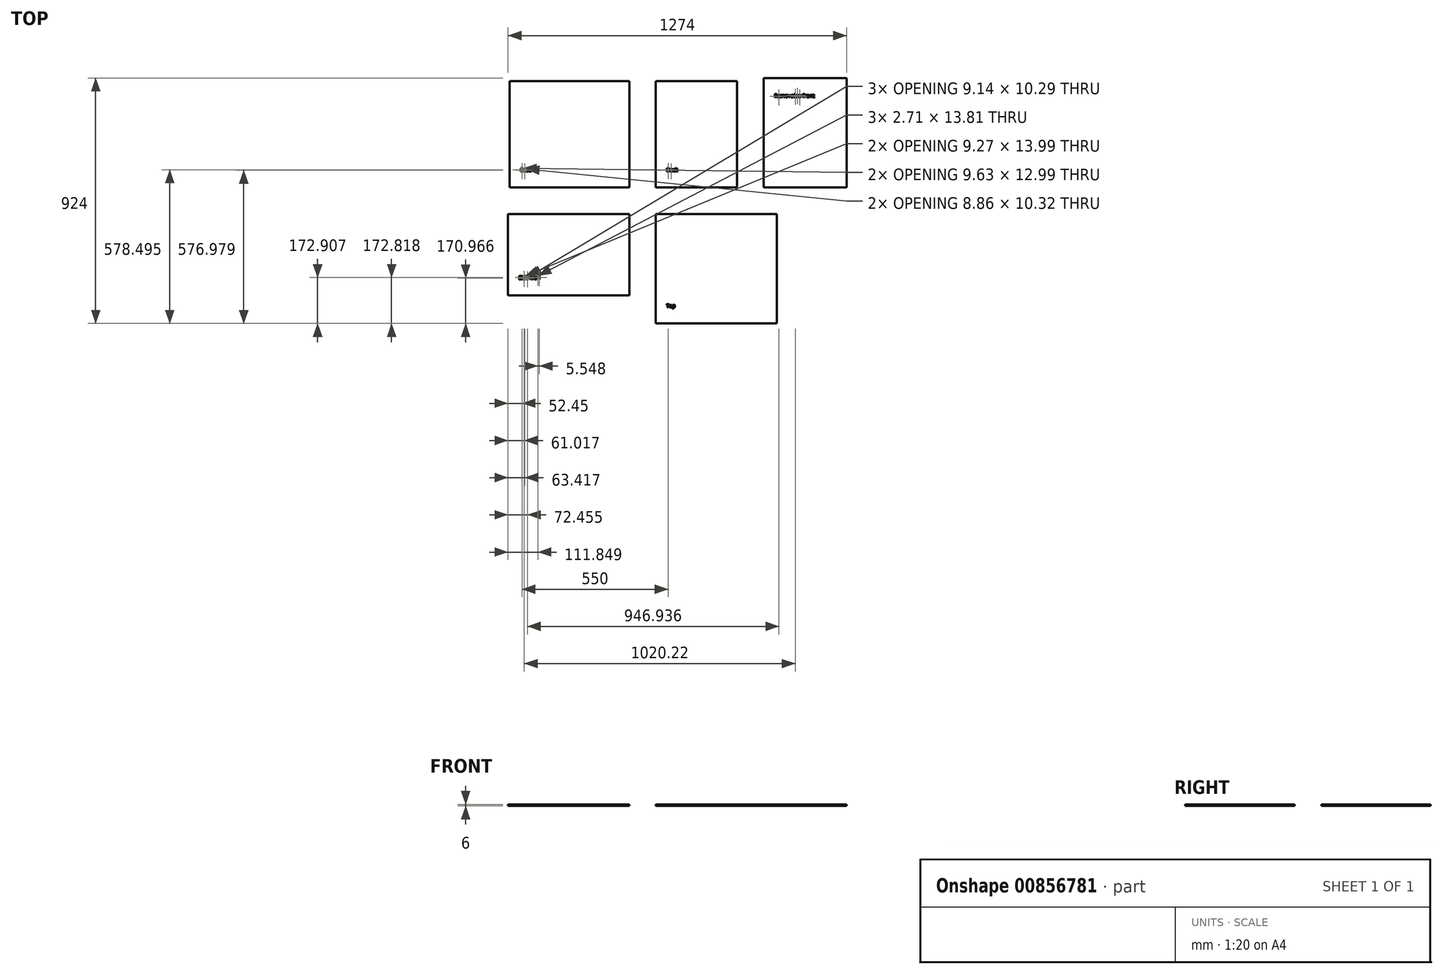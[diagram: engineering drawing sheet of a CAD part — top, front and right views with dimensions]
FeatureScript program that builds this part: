
annotation { "Feature Type Name" : "Feature", "Feature Type Description" : "" }
export const myFeature = defineFeature(function(context is Context, id is Id, definition is map)
    precondition{}
    {
        {
            var Q0;
            Q0=qCreatedBy(makeId("Top.planeOp"),FACE);
            var sketch = newSketch(context, id + "F0", { "sketchPlane" : qUnion([Q0])});
            skLineSegment(sketch, "E0.bottom", {"start": v(-50, 50) * mm, "end": v(-500, 50) * mm});
            skLineSegment(sketch, "E0.top", {"start": v(-50, 450) * mm, "end": v(-500, 450) * mm});
            skLineSegment(sketch, "E0.left", {"start": v(-50, 50) * mm, "end": v(-50, 450) * mm});
            skLineSegment(sketch, "E0.right", {"start": v(-500, 50) * mm, "end": v(-500, 450) * mm});
            skLineSegment(sketch, "E1.bottom", {"start": v(50, 50) * mm, "end": v(356, 50) * mm});
            skLineSegment(sketch, "E1.top", {"start": v(50, 450) * mm, "end": v(356, 450) * mm});
            skLineSegment(sketch, "E1.left", {"start": v(50, 50) * mm, "end": v(50, 450) * mm});
            skLineSegment(sketch, "E1.right", {"start": v(356, 50) * mm, "end": v(356, 450) * mm});
            skLineSegment(sketch, "E2.bottom", {"start": v(-50, -50) * mm, "end": v(-506, -50) * mm});
            skLineSegment(sketch, "E2.top", {"start": v(-50, -356) * mm, "end": v(-506, -356) * mm});
            skLineSegment(sketch, "E2.left", {"start": v(-50, -50) * mm, "end": v(-50, -356) * mm});
            skLineSegment(sketch, "E2.right", {"start": v(-506, -50) * mm, "end": v(-506, -356) * mm});
            skLineSegment(sketch, "E3.bottom", {"start": v(50, -50) * mm, "end": v(506, -50) * mm});
            skLineSegment(sketch, "E3.top", {"start": v(50, -462) * mm, "end": v(506, -462) * mm});
            skLineSegment(sketch, "E3.left", {"start": v(50, -50) * mm, "end": v(50, -462) * mm});
            skLineSegment(sketch, "E3.right", {"start": v(506, -50) * mm, "end": v(506, -462) * mm});
            skLineSegment(sketch, "E4", {"start": v(396, 50) * mm, "end": v(396, 60) * mm, "construction": true});
            skText(sketch, "E5", { "text": "Back", "fontName": "OpenSans-Bold.ttf"});
            skText(sketch, "E6", { "text": "Side wall", "fontName": "OpenSans-Bold.ttf"});
            skText(sketch, "E7", { "text": "Base", "fontName": "OpenSans-Bold.ttf"});
            skText(sketch, "E8", { "text": "Top", "fontName": "OpenSans-Bold.ttf"});
            skLineSegment(sketch, "E9.bottom", {"start": v(456, 50) * mm, "end": v(768, 50) * mm});
            skLineSegment(sketch, "E9.top", {"start": v(456, 462) * mm, "end": v(768, 462) * mm});
            skLineSegment(sketch, "E9.left", {"start": v(456, 50) * mm, "end": v(456, 462) * mm});
            skLineSegment(sketch, "E9.right", {"start": v(768, 50) * mm, "end": v(768, 462) * mm});
            skText(sketch, "E10", { "text": "Removable front", "fontName": "OpenSans-Bold.ttf"});
            const initialGuessF0  = {"E5": [0.09, 0.11, 1, 0, 0.0131], "E6": [-0.466, -0.296, 1, 0, 0.01309], "E7": [-0.46, 0.11, 1, 0, 0.0131], "E8": [0.09, -0.402, 1, 0, 0.0131], "E10": [0.496, 0.38891, 1, 0, 0.01309]};
            skSetInitialGuess(sketch, initialGuessF0);
            skSolve(sketch);
        }
        {
            var Q0;
            Q0=makeQuery(id+"F0.imprint","IMPRINT",FACE,{"disambiguationData":[TD([[makeQuery(id+"F0.imprint","IMPRINT",EDGE,{"derivedFrom":sQuery(id+"F0.wireOp",EDGE,"E0.bottom")}),-1.0]])]});
            extrude(context, id + "F1", {"entities" : qUnion([Q0]), "depth" : 6 * mm, "offsetDistance" : 25 * mm});
        }
        {
            var Q0;
            Q0=makeQuery(id+"F0.imprint","IMPRINT",FACE,{"disambiguationData":[TD([[makeQuery(id+"F0.imprint","IMPRINT",EDGE,{"derivedFrom":sQuery(id+"F0.wireOp",EDGE,"E1.bottom")}),1.0]])]});
            extrude(context, id + "F2", {"entities" : qUnion([Q0]), "depth" : 6 * mm, "offsetDistance" : 25 * mm});
        }
        {
            var Q0;
            Q0=makeQuery(id+"F0.imprint","IMPRINT",FACE,{"disambiguationData":[TD([[makeQuery(id+"F0.imprint","IMPRINT",EDGE,{"derivedFrom":sQuery(id+"F0.wireOp",EDGE,"E2.bottom")}),1.0]])]});
            extrude(context, id + "F3", {"entities" : qUnion([Q0]), "depth" : 6 * mm, "offsetDistance" : 25 * mm});
        }
        {
            var Q0;
            Q0=makeQuery(id+"F0.imprint","IMPRINT",FACE,{"disambiguationData":[TD([[makeQuery(id+"F0.imprint","IMPRINT",EDGE,{"derivedFrom":sQuery(id+"F0.wireOp",EDGE,"E3.bottom")}),-1.0]])]});
            extrude(context, id + "F4", {"entities" : qUnion([Q0]), "depth" : 6 * mm, "offsetDistance" : 25 * mm});
        }
        {
            var Q0;
            Q0=makeQuery(id+"F0.imprint","IMPRINT",FACE,{"disambiguationData":[TD([[makeQuery(id+"F0.imprint","IMPRINT",EDGE,{"derivedFrom":sQuery(id+"F0.wireOp",EDGE,"E9.bottom")}),1.0]])]});
            extrude(context, id + "F5", {"entities" : qUnion([Q0]), "depth" : 6 * mm, "offsetDistance" : 25 * mm});
        }
    });
